# Revit family: O5MA
name_source: partatom
category: Mechanical Equipment
units: mm (PartAtom-declared; Revit-internal decimal feet)

## family parameters
Always vertical = Yes
Cut with Voids When Loaded = No
OmniClass Number = 23.40.40.11.17
OmniClass Title = Refrigerated Cases
Part Type = Normal
Room Calculation Point = No
Round Connector Dimension = Use Radius
Shared = No
Work Plane-Based = Yes

## types (4) — shared parameters
20" Shelf = Yes
Anti-Condensate Heaters Amps = 0 A
Anti-Condensate Heaters Watts = 0 W
BOTTOM ELECTRICAL = Yes
BOTTOM REFRIGERATION PIPING = Yes
BTUH Conventional = 1967
BTUH Parallel = 1680
Certifications = NSF 7, UL471, CSA
Coil Type = ---
DATE = 03/20/2017
DESIGNERS NAME = SHIDDRAMESH
DRAIN PIPING = Yes
Default Elevation = 48"
Defrosts Per Day = 6
Description = Multi-Deck Merchandiser
Discharge Air (°F) = 26 °F
Discharge Air Velocity (FPM) = 225 FPM
EQUIPMENT DESCRIPTION = Multi-Deck Merchandiser
EQUIPMENT MARK = O5MA
Electric Defrost Fail-Safe (Min) = ---
Electric Defrost Termination Temp = 0 °F
Evaporator (°F) = 17 °F
GLASS = Glass
Height = 81 11/16"
High Efficiency Fan Amps = 0 A
High Efficiency Fan Watts = 0 W
Hot Gas Defrost Fail-Safe (Min) = ---
Hot Gas Defrost Termination Temp = 0 °F
Item Description = Multi-Deck Merchandiser
LF STD END = Yes
Legend Number = O5MA
Manufacturer = HILL PHOENIX
Model = O5MA
PAINTED METAL UPPER SHELF = PAINTED SHELVES
REAR REFRIGERATION PIPING = Yes
REFRIGERATION PIPING = COPPER PIPE
RT STD END = Yes
Refgn = 8 3/4"
Run-Off Time (Min) = 45
STAINLESS STEEL = GALVANIZED STEEL
Standard Power Amps = 0 A
Superheat Set Point @ Bulb (°F) = 6 - 8
TOP ELECTRICAL = Yes
TOP REFRIGERATION PIPING = Yes
Timed-Off Defrost Fail-Safe (Min) = -
Timed-Off Defrost Termination Temp = 45 °F
URL = http://www.hillphoenix.com
Width = 43 1/4"
zero-valued in all types: Fans Per Case

## per-type parameters (varying)
| type | CENTER LINE | DRAIN LINE | Defrost (Phase 1) 208 V Amps | Defrost (Phase 1) 208 V Watts | Defrost (Phase 1) 240 V Amps | Defrost (Phase 1) 240 V Watts | High Power (Cornice) Amps | High Power (Cornice) Watts | Length | Length of Cases | Light Length | Lights Per Row | Refrigeration | Standard Power Watts |
| 06' | 36" | 36" | 3 A | 600 W | 3 A | 798 W | 0 A | 30 W | 72" | 72" | 3' | 2 | 28 5/8" | 17 W |
| 08' | 48" | 48" | 4 A | 800 W | 4 A | 1065 W | 0 A | 43 W | 96" | 96" | 4' | 2 | 28 5/8" | 24 W |
| 12' | 72" | 72" | 6 A | 1200 W | 7 A | 1600 W | 1 A | 65 W | 144" | 144" | 4' | 3 | 28 5/8" | 36 W |
| 04' | 24" | 24" | 2 A | 400 W | 2 A | 532 W | 0 A | 22 W | 48" | 72" | 4' | 1 | 22 9/16" | 12 W |

## geometry (parser evidence)
native form markers: Blend x13, Sweep x1
no freeform markers — native parametric forms only
